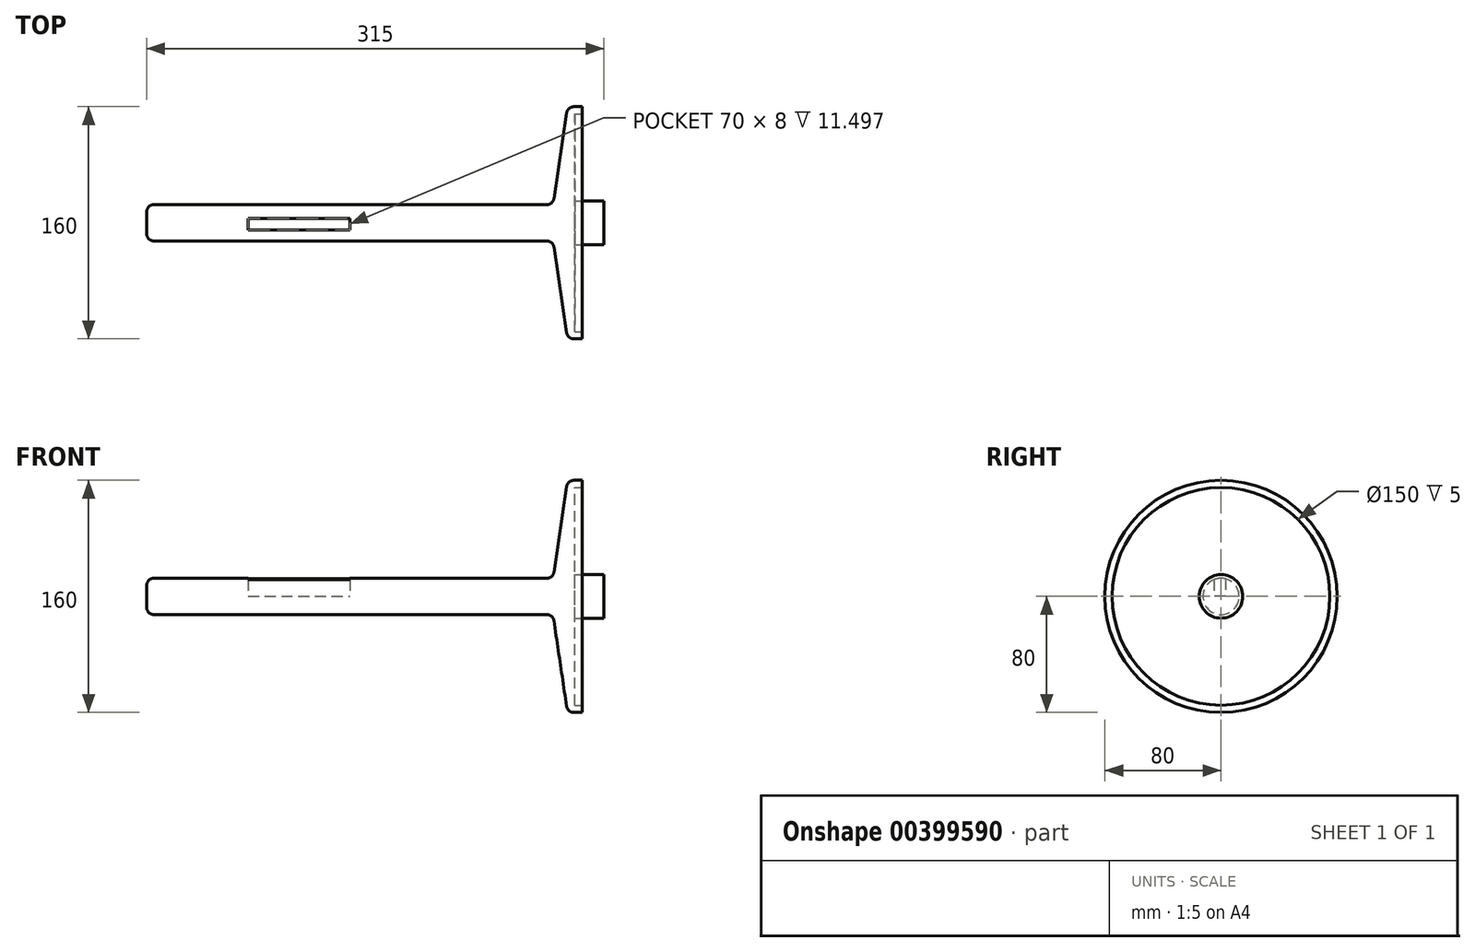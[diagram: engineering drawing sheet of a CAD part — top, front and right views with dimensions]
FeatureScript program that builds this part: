
annotation { "Feature Type Name" : "Feature", "Feature Type Description" : "" }
export const myFeature = defineFeature(function(context is Context, id is Id, definition is map)
    precondition{}
    {
        {
            var Q0;
            Q0=qCreatedBy(makeId("Front.planeOp"),FACE);
            var sketch = newSketch(context, id + "F0", { "sketchPlane" : qUnion([Q0])});
            skLineSegment(sketch, "E0", {"start": v(0, 0) * mm, "end": v(0, 12.5) * mm});
            skLineSegment(sketch, "E1", {"start": v(0, 12.5) * mm, "end": v(280, 12.5) * mm});
            skLineSegment(sketch, "E2", {"start": v(280, 12.5) * mm, "end": v(290, 80) * mm});
            skLineSegment(sketch, "E3", {"start": v(290, 80) * mm, "end": v(300, 80) * mm});
            skLineSegment(sketch, "E4", {"start": v(300, 80) * mm, "end": v(300, 75) * mm});
            skLineSegment(sketch, "E5", {"start": v(295, 0) * mm, "end": v(0, 0) * mm});
            skLineSegment(sketch, "E6.0", {"start": v(295, 75) * mm, "end": v(300, 75) * mm});
            skLineSegment(sketch, "E7.0", {"start": v(295, 75) * mm, "end": v(295, 15) * mm});
            skPoint(sketch, "E8.orphan", {"position": v(300, 0) * mm});
            skLineSegment(sketch, "E9", {"start": v(295, 0) * mm, "end": v(315, 0) * mm});
            skLineSegment(sketch, "E10", {"start": v(315, 0) * mm, "end": v(315, 15) * mm});
            skLineSegment(sketch, "E11", {"start": v(315, 15) * mm, "end": v(295, 15) * mm});
            skSolve(sketch);
        }
        {
            var Q0;
            Q0=makeQuery(id+"F0.imprint","IMPRINT",FACE,{"disambiguationData":[TD([[makeQuery(id+"F0.imprint","IMPRINT",EDGE,{"derivedFrom":sQuery(id+"F0.wireOp",EDGE,"E0")}),-1.0]])]});
            var Q1;
            Q1=sQuery(id+"F0.wireOp",EDGE,"E5");
            revolve(context, id + "F1", {"entities" : qUnion([Q0]), "axis" : qUnion([Q1]), "revolveType" : RevolveType.ONE_DIRECTION, "angle" : 360 * degree});
        }
        {
            var Q0;
            Q0=qCreatedBy(makeId("Top.planeOp"),FACE);
            var sketch = newSketch(context, id + "F2", { "sketchPlane" : qUnion([Q0])});
            skLineSegment(sketch, "E12.bottom", {"start": v(70, 3.1) * mm, "end": v(140, 3.1) * mm});
            skLineSegment(sketch, "E12.top", {"start": v(70, -4.9) * mm, "end": v(140, -4.9) * mm});
            skLineSegment(sketch, "E12.left", {"start": v(70, 3.1) * mm, "end": v(70, -4.9) * mm});
            skLineSegment(sketch, "E12.right", {"start": v(140, 3.1) * mm, "end": v(140, -4.9) * mm});
            skSolve(sketch);
        }
        {
            var Q0;
            Q0 = qSketchRegion(id + "F2", true);
            extrude(context, id + "F3", {"entities" : qUnion([Q0]), "operationType" : NewBodyOperationType.REMOVE, "endBound" : BoundingType.UP_TO_NEXT, "depth" : 25 * mm});
        }
        {
            var Q0;
            Q0=makeQuery(id+"F1.opRevolve","SWEPT_EDGE",EDGE,{"disambiguationData":[OSD([sQuery(id+"F0.wireOp",EDGE,"E2"),sQuery(id+"F0.wireOp",EDGE,"E3")])]});
            var Q1;
            Q1=makeQuery(id+"F1.opRevolve","SWEPT_EDGE",EDGE,{"disambiguationData":[OSD([sQuery(id+"F0.wireOp",EDGE,"E1"),sQuery(id+"F0.wireOp",EDGE,"E2")])]});
            fillet(context, id + "F4", {"entities" : qUnion([Q0, Q1]), "radius" : 5 * mm, "tangentPropagation" : true, "allowEdgeOverflow" : false});
        }
        {
            var Q0;
            Q0=makeQuery(id+"F1.opRevolve","SWEPT_EDGE",EDGE,{"disambiguationData":[OSD([sQuery(id+"F0.wireOp",EDGE,"E0"),sQuery(id+"F0.wireOp",EDGE,"E1")])]});
            fillet(context, id + "F5", {"entities" : qUnion([Q0]), "radius" : 5 * mm, "tangentPropagation" : true, "allowEdgeOverflow" : false});
        }
    });
